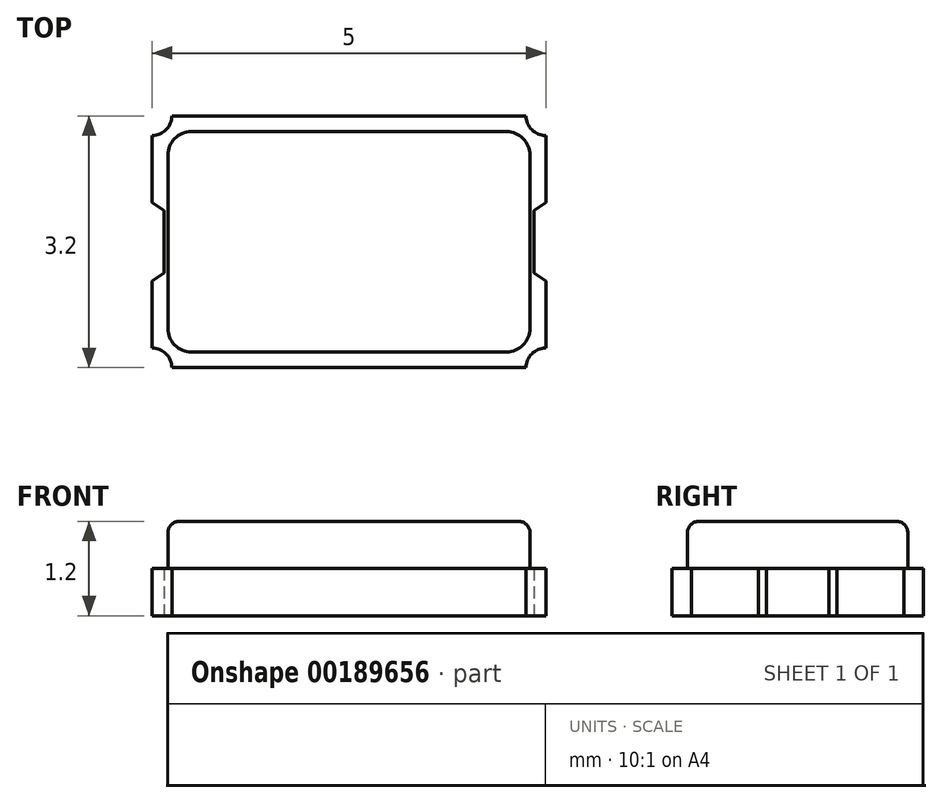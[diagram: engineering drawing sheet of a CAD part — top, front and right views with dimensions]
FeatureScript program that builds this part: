
annotation { "Feature Type Name" : "Feature", "Feature Type Description" : "" }
export const myFeature = defineFeature(function(context is Context, id is Id, definition is map)
    precondition{}
    {
        {
            var Q0;
            Q0=qCreatedBy(makeId("Top.planeOp"),FACE);
            var sketch = newSketch(context, id + "F0", { "sketchPlane" : qUnion([Q0])});
            skLineSegment(sketch, "E0.bottom", {"start": v(0, 0) * mm, "end": v(2.35, 0) * mm});
            skLineSegment(sketch, "E0.top", {"start": v(0, 1.6) * mm, "end": v(2.25, 1.6) * mm});
            skLineSegment(sketch, "E0.left", {"start": v(0, 0) * mm, "end": v(0, 1.6) * mm});
            skLineSegment(sketch, "E0.right", {"start": v(2.5, 0.5) * mm, "end": v(2.5, 1.35) * mm});
            skArc(sketch, "E1", {"start": v(2.25, 1.6) * mm, "mid": v(2.32, 1.42) * mm, "end": v(2.5, 1.35) * mm});
            skLineSegment(sketch, "E2", {"start": v(2.5, 0.5) * mm, "end": v(2.35, 0.4) * mm});
            skLineSegment(sketch, "E3", {"start": v(2.35, 0.4) * mm, "end": v(2.35, 0) * mm});
            skPoint(sketch, "E4.orphan", {"position": v(2.5, 0) * mm});
            skSolve(sketch);
        }
        {
            var Q0;
            Q0=qSketchRegion(id+"F0",true);
            extrude(context, id + "F1", {"entities" : qUnion([Q0]), "depth" : 0.6 * mm});
        }
        {
            var Q0;
            Q0=makeQuery(id+"F1.opExtrude","CAP_FACE",FACE,{"disambiguationData":[OSD([sQuery(id+"F0.wireOp",EDGE,"E0.bottom"),sQuery(id+"F0.wireOp",EDGE,"E0.top"),sQuery(id+"F0.wireOp",EDGE,"E0.left"),sQuery(id+"F0.wireOp",EDGE,"E0.right"),sQuery(id+"F0.wireOp",EDGE,"E1")])],"isStart":false});
            var sketch = newSketch(context, id + "F2", { "sketchPlane" : qUnion([Q0])});
            skLineSegment(sketch, "E5.bottom", {"start": v(0, 0) * mm, "end": v(2.3, 0) * mm});
            skLineSegment(sketch, "E5.top", {"start": v(0, 1.4) * mm, "end": v(2, 1.4) * mm});
            skLineSegment(sketch, "E5.left", {"start": v(0, 0) * mm, "end": v(0, 1.4) * mm});
            skLineSegment(sketch, "E5.right", {"start": v(2.3, 0) * mm, "end": v(2.3, 1.1) * mm});
            skPoint(sketch, "E6.visualSharp", {"position": v(2.3, 1.4) * mm});
            skArc(sketch, "E6.filletArc", {"start": v(2.3, 1.1) * mm, "mid": v(2.21, 1.31) * mm, "end": v(2, 1.4) * mm});
            skSolve(sketch);
        }
        {
            var Q0;
            Q0=qSketchRegion(id+"F2",true);
            extrude(context, id + "F3", {"entities" : qUnion([Q0]), "operationType" : NewBodyOperationType.ADD, "depth" : 0.6 * mm});
        }
        {
            var Q0;
            Q0=makeQuery(id+"F1.opExtrude","SWEPT_BODY",BODY,{"disambiguationData":[OSD([sQuery(id+"F0.wireOp",EDGE,"E0.bottom"),sQuery(id+"F0.wireOp",EDGE,"E0.top"),sQuery(id+"F0.wireOp",EDGE,"E0.left"),sQuery(id+"F0.wireOp",EDGE,"E0.right"),sQuery(id+"F0.wireOp",EDGE,"E1")])]});
            var Q1;
            Q1=makeQuery(id+"F3.boolean.opBoolean","MERGE",FACE,{"derivedFrom":[makeQuery(id+"F1.opExtrude","SWEPT_FACE",FACE,{"disambiguationData":[OSD([sQuery(id+"F0.wireOp",EDGE,"E0.left")])]}),makeQuery(id+"F3.opExtrude","SWEPT_FACE",FACE,{"disambiguationData":[OSD([sQuery(id+"F2.wireOp",EDGE,"E5.left")])]})]});
            mirror(context, id + "F4", {"operationType" : NewBodyOperationType.ADD, "entities" : qUnion([Q0]), "mirrorPlane" : qUnion([Q1])});
        }
        {
            var Q0;
            Q0=makeQuery(id+"F1.opExtrude","SWEPT_BODY",BODY,{"disambiguationData":[OSD([sQuery(id+"F0.wireOp",EDGE,"E0.bottom"),sQuery(id+"F0.wireOp",EDGE,"E0.top"),sQuery(id+"F0.wireOp",EDGE,"E0.left"),sQuery(id+"F0.wireOp",EDGE,"E0.right"),sQuery(id+"F0.wireOp",EDGE,"E1")])]});
            var Q1;
            {var subQ0=makeQuery(id+"F3.boolean.opBoolean","MERGE",FACE,{"derivedFrom":[makeQuery(id+"F1.opExtrude","SWEPT_FACE",FACE,{"disambiguationData":[OSD([sQuery(id+"F0.wireOp",EDGE,"E0.bottom")])]}),makeQuery(id+"F3.opExtrude","SWEPT_FACE",FACE,{"disambiguationData":[OSD([sQuery(id+"F2.wireOp",EDGE,"E5.bottom")])]})]});Q1=makeQuery(id+"F4.boolean.opBoolean","MERGE",FACE,{"derivedFrom":[subQ0,makeQuery(id+"F4.opPattern","COPY",FACE,{"derivedFrom":subQ0,"instanceName":"1"})]});}
            mirror(context, id + "F5", {"operationType" : NewBodyOperationType.ADD, "entities" : qUnion([Q0]), "mirrorPlane" : qUnion([Q1])});
        }
        {
            var Q0;
            {var subQ0=makeQuery(id+"F3.opExtrude","CAP_FACE",FACE,{"disambiguationData":[OSD([sQuery(id+"F2.wireOp",EDGE,"E5.bottom"),sQuery(id+"F2.wireOp",EDGE,"E5.top"),sQuery(id+"F2.wireOp",EDGE,"E5.left"),sQuery(id+"F2.wireOp",EDGE,"E5.right"),sQuery(id+"F2.wireOp",EDGE,"E6.filletArc")])],"isStart":false});var subQ1=makeQuery(id+"F4.boolean.opBoolean","MERGE",FACE,{"derivedFrom":[subQ0,makeQuery(id+"F4.opPattern","COPY",FACE,{"derivedFrom":subQ0,"instanceName":"1"})]});Q0=makeQuery(id+"F5.boolean.opBoolean","MERGE",FACE,{"derivedFrom":[subQ1,makeQuery(id+"F5.opPattern","COPY",FACE,{"derivedFrom":subQ1,"instanceName":"1"})]});}
            fillet(context, id + "F6", {"entities" : qUnion([Q0]), "radius" : 0.15 * mm, "tangentPropagation" : true, "allowEdgeOverflow" : false});
        }
    });
